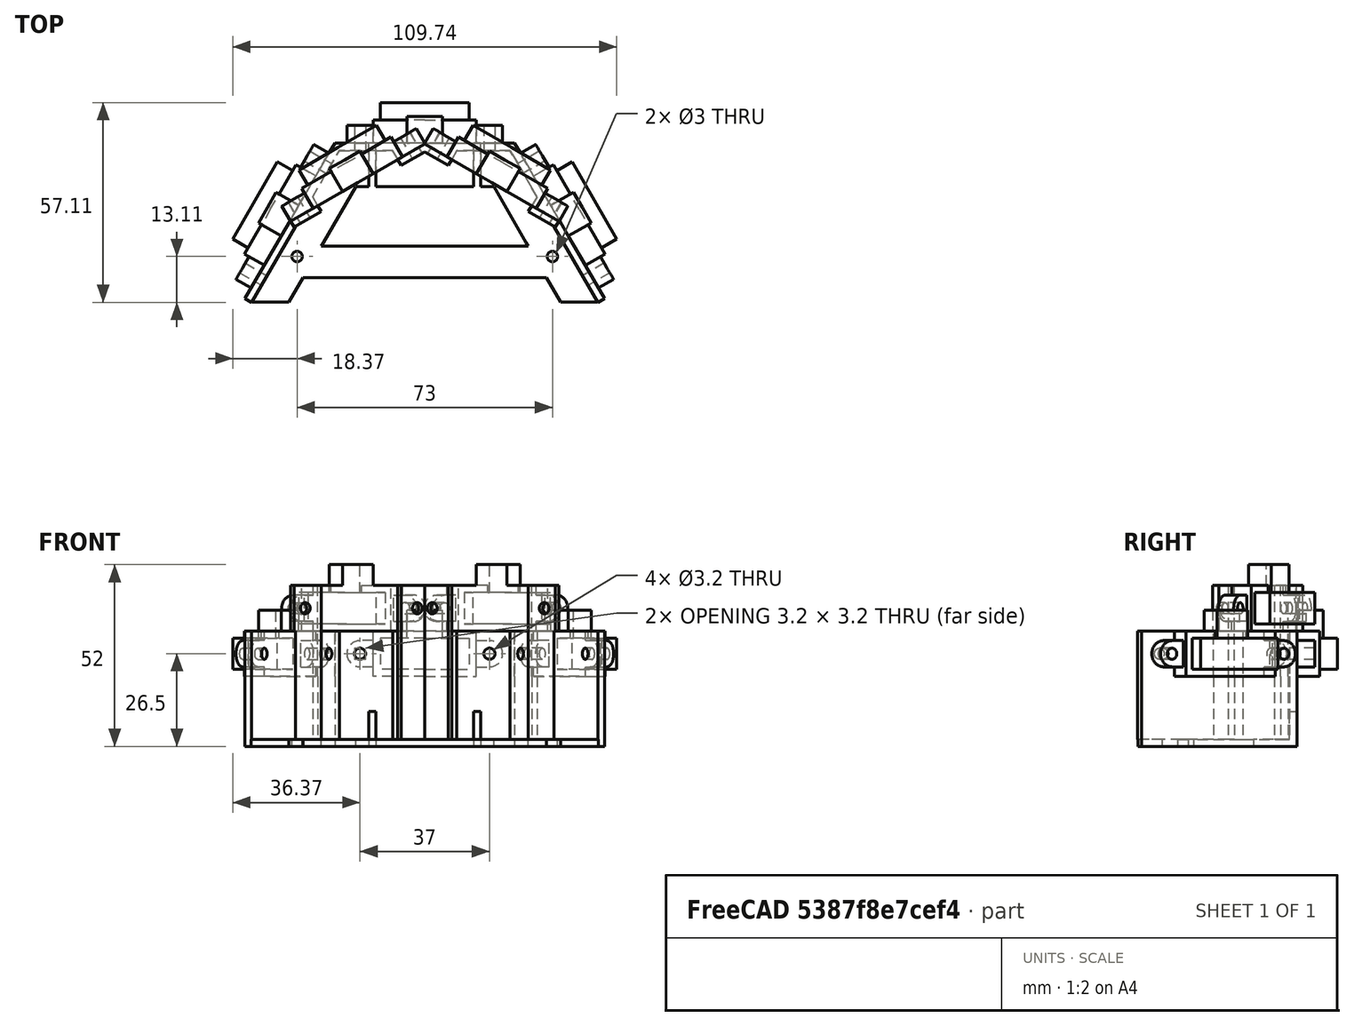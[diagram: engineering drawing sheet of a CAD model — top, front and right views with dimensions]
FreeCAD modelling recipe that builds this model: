
FCSTD DOCUMENT  (FreeCAD 0.15R4671 (Git))
Label: ir_sensor_holder
License: All rights reserved
LicenseURL: http://en.wikipedia.org/wiki/All_rights_reserved
objects: Part::MultiFuse×19, Part::Box×17, Part::Cut×11, Part::Mirroring×10, Part::Cylinder×7, Part::FeaturePython×5, Part::Feature×3, Part::Extrusion×2
note: 74 computed .brp shape members not serialized (recipe doc carries the construction recipe); baked Part::Feature solids carry a one-line shape summary decoded from their .brp

FEATURE [Part::Box] Box004  label="Cubo004"
  Height = 13
  Length = 14.75
  Width = 6.5
FEATURE [Part::Box] Box005  label="Cubo005"
  Height = 7.5
  Length = 18.5
  Placement = pos=(0,0,2.75) rot=(0,0,1;0rad)
  Width = 5
FEATURE [Part::Cylinder] Cylinder  label="Cilindro"
  Angle = 360
  Height = 5
  Placement = pos=(18.5,5,6.5) rot=(1,0,0;1.5708rad)
  Radius = 3.75
FEATURE [Part::Cylinder] Cylinder001  label="Cilindro001"
  Angle = 360
  Height = 5
  Placement = pos=(18.5,5,6.5) rot=(1,0,0;1.5708rad)
  Radius = 1.6
FEATURE [Part::MultiFuse] Fusion
  Shapes = -> [Cylinder,Box005]
FEATURE [Part::Cut] Cut
  Base = -> Fusion
  Tool = -> Cylinder001
FEATURE [Part::Box] Box006  label="Cubo006"
  Height = 9
  Length = 12.75
  Placement = pos=(0,6,2) rot=(0,0,1;0rad)
  Width = 5.5
FEATURE [Part::Box] Box007  label="Cubo007"
  Height = 8
  Length = 5.05
  Placement = pos=(0,0,11) rot=(0,0,1;0rad)
  Width = 7.5
FEATURE [Part::MultiFuse] Fusion001
  Shapes = -> [Box007,Box004,Box006,Cut]
FEATURE [Part::Mirroring] Part__Mirroring  label="Fusion001 (Mirror #1)"
  Base = (0,0,0)
  Normal = (0,0,1)
  Source = -> Fusion001
FEATURE [Part::MultiFuse] Fusion002022  label="IR_sensor_SHARP"
  Placement = pos=(0,44.5,0) rot=(0,0,1;0rad)
  Shapes = -> [Part__Mirroring,Fusion001]
FEATURE [Part::FeaturePython] Array  # Draft array (typed FeaturePython)
  Angle = 120
  ArrayType = 1
  Axis = (0,0,1)
  Base = -> Fusion002022
  Center = (0,0,0)
  Fuse = false
  IntervalAxis = (0,0,0)
  IntervalX = (1,0,0)
  IntervalY = (0,1,0)
  IntervalZ = (0,0,0)
  NumberPolar = 3
  NumberX = 2
  NumberY = 2
  NumberZ = 1
  Placement = pos=(0,0,0) rot=(0,0,-1;1.0472rad)
FEATURE [Part::Box] Box  label="Cubo031"
  Height = 13
  Length = 14.75
  Width = 6.5
FEATURE [Part::Box] Box031  label="Cubo032"
  Height = 7.5
  Length = 18.5
  Placement = pos=(0,0,2.75) rot=(0,0,1;0rad)
  Width = 5
FEATURE [Part::Cylinder] Cylinder002  label="Cilindro002"
  Angle = 360
  Height = 5
  Placement = pos=(18.5,5,6.5) rot=(1,0,0;1.5708rad)
  Radius = 3.75
FEATURE [Part::Cylinder] Cylinder003  label="Cilindro003"
  Angle = 360
  Height = 5
  Placement = pos=(18.5,5,6.5) rot=(1,0,0;1.5708rad)
  Radius = 1.6
FEATURE [Part::MultiFuse] Fusion002023
  Shapes = -> [Cylinder002,Box031]
FEATURE [Part::Cut] Cut001
  Base = -> Fusion002023
  Tool = -> Cylinder003
FEATURE [Part::Box] Box032  label="Cubo033"
  Height = 9
  Length = 12.75
  Placement = pos=(0,6,2) rot=(0,0,1;0rad)
  Width = 5.5
FEATURE [Part::Box] Box033  label="Cubo034"
  Height = 8
  Length = 5.05
  Placement = pos=(0,0,11) rot=(0,0,1;0rad)
  Width = 7.5
FEATURE [Part::MultiFuse] Fusion002024
  Shapes = -> [Box033,Box,Box032,Cut001]
FEATURE [Part::Mirroring] Part__Mirroring001  label="Fusion001 (Mirror #1)001"
  Base = (0,0,0)
  Normal = (0,0,1)
  Source = -> Fusion002024
FEATURE [Part::MultiFuse] Fusion002025  label="IR_sensor_SHARP001"
  Placement = pos=(0,38.3,13) rot=(0,0,1;0rad)
  Shapes = -> [Part__Mirroring001,Fusion002024]
FEATURE [Part::FeaturePython] Array001  # Draft array (typed FeaturePython)
  Angle = 60
  ArrayType = 1
  Axis = (0,0,1)
  Base = -> Fusion002025
  Center = (0,0,0)
  Fuse = false
  IntervalAxis = (0,0,0)
  IntervalX = (1,0,0)
  IntervalY = (0,1,0)
  IntervalZ = (0,0,0)
  NumberPolar = 2
  NumberX = 2
  NumberY = 2
  NumberZ = 1
  Placement = pos=(0,0,0) rot=(0,0,-1;0.523599rad)
FEATURE [Part::MultiFuse] Fusion002026  label="Sensors_union"
  Placement = pos=(0,1,20) rot=(0,0,1;0rad)
  Shapes = -> [Array,Array001]
FEATURE [Part::Box] Box034  label="Cubo"
  Height = 13
  Length = 25.7
  Placement = pos=(0,42.3,0) rot=(0,0,1;0rad)
  Width = 2.2
FEATURE [Part::Cylinder] Cylinder004  label="Cilindro004"
  Angle = 360
  Height = 10
  Placement = pos=(18.5,50,6.5) rot=(1,0,0;1.5708rad)
  Radius = 1.6
FEATURE [Part::Cut] Cut002
  Base = -> Box034
  Tool = -> Cylinder004
FEATURE [Part::Mirroring] Part__Mirroring002  label="Cut002 (Mirror #3)"
  Base = (0,0,0)
  Normal = (1,0,0)
  Source = -> Cut002
FEATURE [Part::MultiFuse] Fusion002027
  Shapes = -> [Cut002,Part__Mirroring002]
FEATURE [Part::Box] Box035  label="Cubo035"
  Height = 26
  Length = 22.13
  Placement = pos=(0,42.5,0) rot=(0,0,1;0rad)
  Width = 2
FEATURE [Part::Cylinder] Cylinder005  label="Cilindro005"
  Angle = 360
  Height = 10
  Placement = pos=(18.5,50,6.5) rot=(1,0,0;1.5708rad)
  Radius = 1.6
FEATURE [Part::Cut] Cut003
  Base = -> Box035
  Placement = pos=(0,-2,0) rot=(0,0,1;0rad)
  Tool = -> Cylinder005
FEATURE [Part::Box] Box036  label="Cubo036"
  Height = 26
  Length = 13.2
  Placement = pos=(0,40.5,0) rot=(0,0,1;0rad)
  Width = 4
FEATURE [Part::Cut] Cut004
  Base = -> Cut003
  Placement = pos=(0,0,26) rot=(0,1,0;3.14159rad)
  Tool = -> Box036
FEATURE [Part::Feature] Face
  shape: bbox 7.295 x 5.256 x 2e-07 mm, 1 faces, 0 solids (baked)
FEATURE [Part::Extrusion] Extrude
  Base = -> Face
  Dir = (0,0,13)
  Solid = true
FEATURE [Part::MultiFuse] Fusion002028
  Shapes = -> [Extrude,Cut004]
FEATURE [Part::Mirroring] Part__Mirroring003  label="Fusion002028 (Mirror #4)"
  Base = (0,0,0)
  Normal = (1,0,0)
  Source = -> Fusion002028
FEATURE [Part::MultiFuse] Fusion002029
  Placement = pos=(0,-4.2,0) rot=(0,0,1;0rad)
  Shapes = -> [Part__Mirroring003,Fusion002028]
FEATURE [Part::FeaturePython] Array003  # Draft array (typed FeaturePython)
  Angle = 60
  ArrayType = 1
  Axis = (0,0,1)
  Base = -> Fusion002029
  Center = (0,0,0)
  Fuse = false
  IntervalAxis = (0,0,0)
  IntervalX = (1,0,0)
  IntervalY = (0,1,0)
  IntervalZ = (0,0,0)
  NumberPolar = 2
  NumberX = 2
  NumberY = 2
  NumberZ = 1
  Placement = pos=(0,1,20) rot=(0,0,-1;0.523599rad)
FEATURE [Part::Cylinder] Cylinder006  label="Cilindro006"
  Angle = 360
  Height = 10
  Placement = pos=(36.5,13,-2) rot=(0,0,1;0rad)
  Radius = 1.5
FEATURE [Part::Box] Box037  label="Cubo037"
  Height = 2
  Length = 25
  Width = 12
FEATURE [Part::Box] Box038  label="Cubo038"
  Height = 2
  Length = 70
  Placement = pos=(-35,7,0) rot=(0,0,1;0rad)
  Width = 9
FEATURE [Part::Mirroring] Part__Mirroring005  label="Cilindro006 (Mirror #6)"
  Base = (0,0,0)
  Normal = (1,0,0)
  Source = -> Cylinder006
FEATURE [Part::MultiFuse] Fusion002031
  Shapes = -> [Cylinder006,Part__Mirroring005]
FEATURE [Part::Box] Box039  label="Cubo039"
  Height = 10
  Length = 2
  Placement = pos=(14,32,0) rot=(0,0,1;0rad)
  Width = 14
FEATURE [Part::Mirroring] Part__Mirroring004  label="Cubo037 (Mirror #5)"
  Base = (0,0,0)
  Normal = (1,0,0)
  Source = -> Box037
FEATURE [Part::MultiFuse] Fusion002030
  Placement = pos=(0,33,0) rot=(0,0,1;0rad)
  Shapes = -> [Box037,Part__Mirroring004]
FEATURE [Part::Mirroring] Part__Mirroring006  label="Cubo039 (Mirror #7)"
  Base = (0,0,0)
  Normal = (1,0,0)
  Source = -> Box039
FEATURE [Part::Box] Box040  label="Cubo040"
  Height = 2
  Length = 25
  Width = 11
FEATURE [Part::Mirroring] Part__Mirroring007  label="Cubo037 (Mirror #5)001"
  Base = (0,0,0)
  Normal = (1,0,0)
  Source = -> Box040
FEATURE [Part::MultiFuse] Fusion002032
  Placement = pos=(29,17,0) rot=(0,0,-1;1.0472rad)
  Shapes = -> [Box040,Part__Mirroring007]
FEATURE [Part::Cut] Cut005
  Base = -> Fusion002030
  Tool = -> Part__Mirroring006
FEATURE [Part::Cut] Cut006
  Base = -> Cut005
  Tool = -> Box039
FEATURE [Part::Box] Box041  label="Cubo041"
  Height = 10
  Length = 2
  Placement = pos=(14,32,0) rot=(0,0,1;0rad)
  Width = 14
FEATURE [Part::Mirroring] Part__Mirroring008  label="Cubo039 (Mirror #7)001"
  Base = (0,0,0)
  Normal = (1,0,0)
  Source = -> Box041
FEATURE [Part::Mirroring] Part__Mirroring009  label="Fusion002032 (Mirror #10)"
  Base = (0,0,0)
  Normal = (1,0,0)
  Source = -> Fusion002032
FEATURE [Part::Box] Box042  label="Cubo042"
  Height = 2
  Length = 109
  Placement = pos=(-52,-9,0) rot=(0,0,1;0rad)
  Width = 9
FEATURE [Part::FeaturePython] Array002  # Draft array (typed FeaturePython)
  Angle = 120
  ArrayType = 1
  Axis = (0,0,1)
  Base = -> Fusion002027
  Center = (0,0,0)
  Fuse = false
  IntervalAxis = (0,0,0)
  IntervalX = (1,0,0)
  IntervalY = (0,1,0)
  IntervalZ = (0,0,0)
  NumberPolar = 3
  NumberX = 2
  NumberY = 2
  NumberZ = 1
  Placement = pos=(0,1,20) rot=(0,0,-1;1.0472rad)
FEATURE [Part::FeaturePython] Facebinder  # WARN: FeaturePython — macro-defined, semantics opaque (R4)
  Faces = -> [Array002,Array003]
FEATURE [Part::Extrusion] Extrude002
  Base = -> Facebinder
  Dir = (0,0,-20)
  Solid = false
FEATURE [Part::Cut] Cut007
  Base = -> Extrude002
  Tool = -> Box039
FEATURE [Part::MultiFuse] Fusion002033
  Shapes = -> [Cut006,Cut007]
FEATURE [Part::Cut] Cut008
  Base = -> Fusion002033
  Tool = -> Part__Mirroring008
FEATURE [Part::MultiFuse] Fusion002035
  Shapes = -> [Fusion002032,Part__Mirroring009,Cut008]
FEATURE [Part::MultiFuse] Fusion002036
  Shapes = -> [Fusion002035,Box038]
FEATURE [Part::Cut] Cut009
  Base = -> Fusion002036
  Tool = -> Box042
FEATURE [Part::Cut] Cut010  label="p1_base"
  Base = -> Cut009
  Tool = -> Fusion002031
FEATURE [Part::Feature] Array002001  label="Array004"
  shape: bbox 102.8 x 45.61 x 13 mm, 24 faces, 3 solids (baked)
FEATURE [Part::MultiFuse] Fusion002037  label="p2_sensor_low"
  Shapes = -> [Array002001,Array002]
FEATURE [Part::Feature] Array003001  label="Array005"
  shape: bbox 76.63 x 23.86 x 26 mm, 44 faces, 4 solids (baked)
FEATURE [Part::MultiFuse] Fusion002038  label="p3_sensor_high"
  Shapes = -> [Array003001,Array003]
FEATURE [Part::MultiFuse] Fusion002039  label="sensors_holder_union"
  Shapes = -> [Fusion002038,Cut010,Fusion002037]
